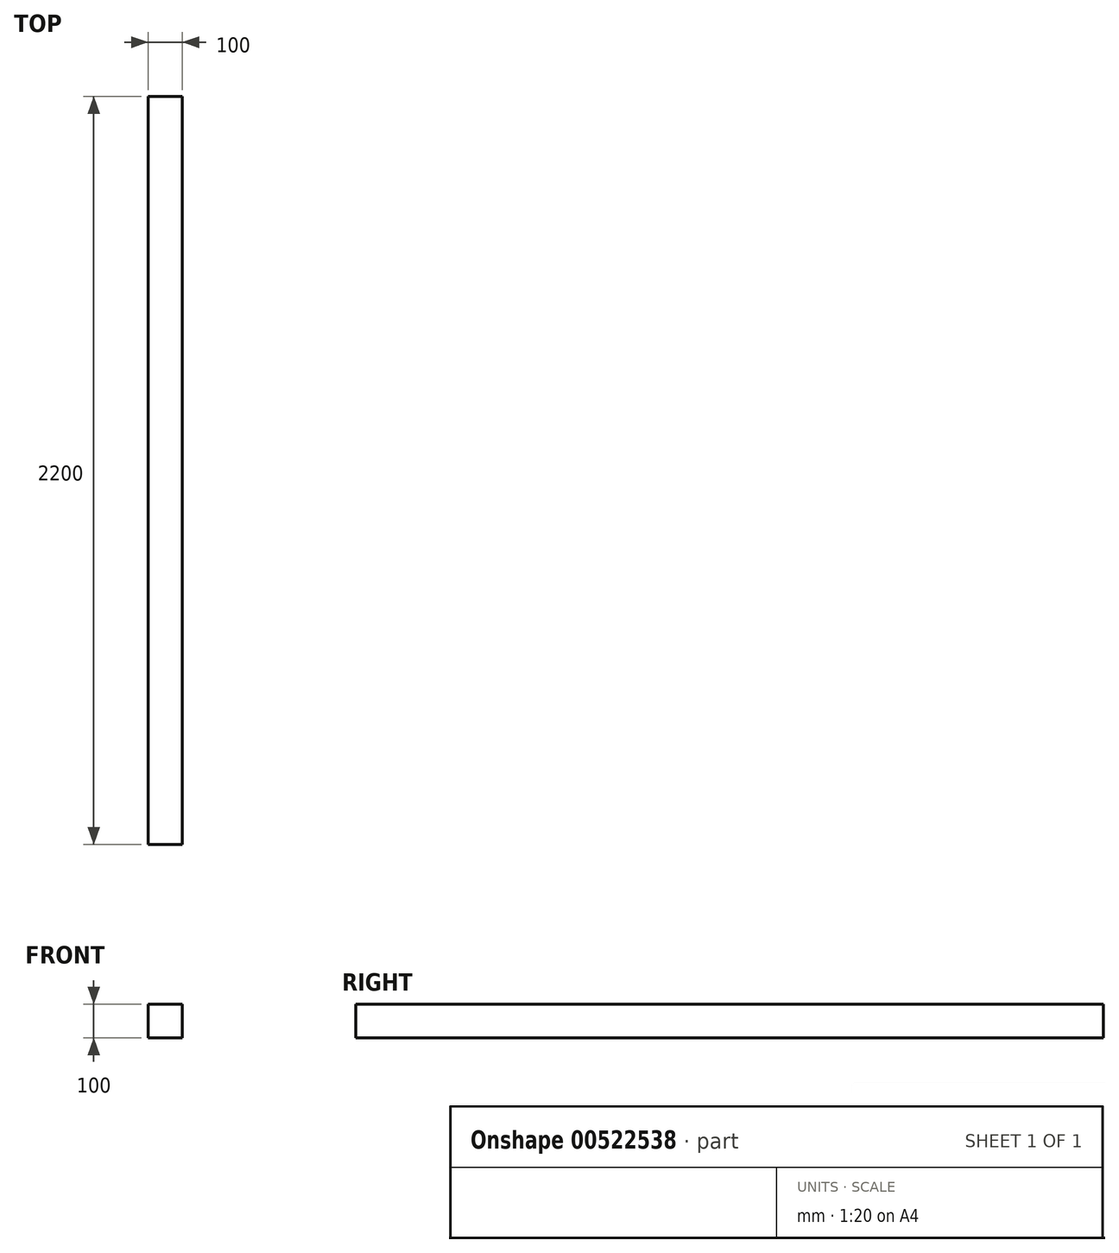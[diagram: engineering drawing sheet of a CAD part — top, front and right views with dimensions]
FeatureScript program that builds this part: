
annotation { "Feature Type Name" : "Feature", "Feature Type Description" : "" }
export const myFeature = defineFeature(function(context is Context, id is Id, definition is map)
    precondition{}
    {
        {
            var Q0;
            Q0=qCreatedBy(makeId("Front.planeOp"),FACE);
            var sketch = newSketch(context, id + "F0", { "sketchPlane" : qUnion([Q0])});
            skLineSegment(sketch, "E0.bottom", {"start": v(-118.75, 94.8) * mm, "end": v(-18.75, 94.8) * mm});
            skLineSegment(sketch, "E0.top", {"start": v(-118.75, -5.2) * mm, "end": v(-18.75, -5.2) * mm});
            skLineSegment(sketch, "E0.left", {"start": v(-118.75, 94.8) * mm, "end": v(-118.75, -5.2) * mm});
            skLineSegment(sketch, "E0.right", {"start": v(-18.75, 94.8) * mm, "end": v(-18.75, -5.2) * mm});
            skSolve(sketch);
        }
        {
            var Q0;
            Q0 = qSketchRegion(id + "F0", true);
            extrude(context, id + "F1", {"entities" : qUnion([Q0]), "depth" : 2200 * mm, "offsetDistance" : 25 * mm});
        }
    });
